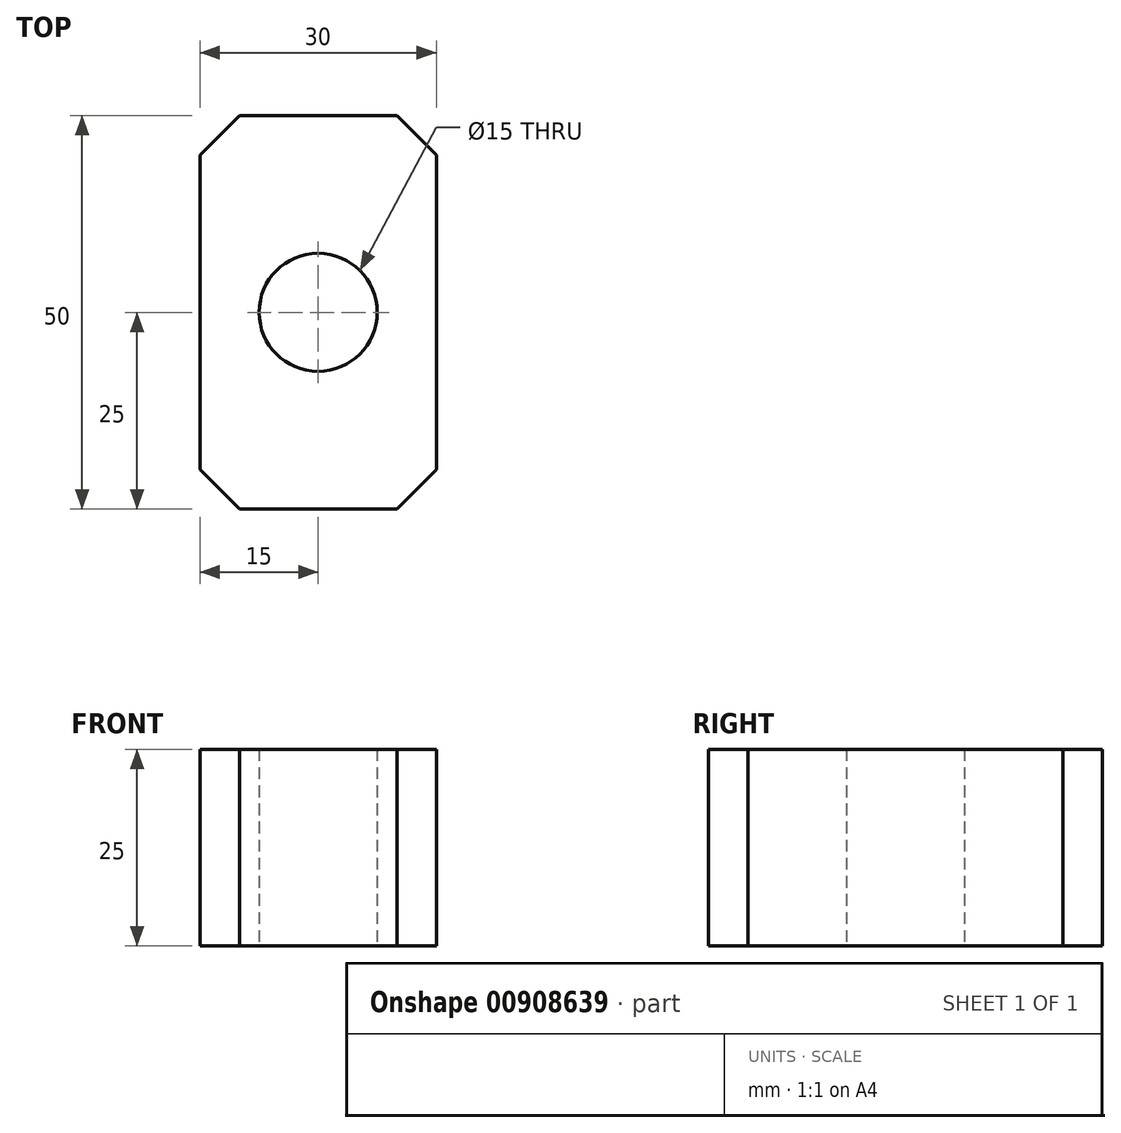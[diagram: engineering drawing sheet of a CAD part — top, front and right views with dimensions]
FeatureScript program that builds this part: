
annotation { "Feature Type Name" : "Feature", "Feature Type Description" : "" }
export const myFeature = defineFeature(function(context is Context, id is Id, definition is map)
    precondition{}
    {
        {
            var Q0;
            Q0=qCreatedBy(makeId("Top.planeOp"),FACE);
            var sketch = newSketch(context, id + "F0", { "sketchPlane" : qUnion([Q0])});
            skLineSegment(sketch, "E0.bottom", {"start": v(-15, 25) * mm, "end": v(15, 25) * mm});
            skLineSegment(sketch, "E0.top", {"start": v(-15, -25) * mm, "end": v(15, -25) * mm});
            skLineSegment(sketch, "E0.left", {"start": v(-15, 25) * mm, "end": v(-15, -25) * mm});
            skLineSegment(sketch, "E0.right", {"start": v(15, 25) * mm, "end": v(15, -25) * mm});
            skLineSegment(sketch, "E1", {"start": v(-15, 25) * mm, "end": v(15, -25) * mm, "construction": true});
            skCircle(sketch, "E2", {"center": v(0, 0) * mm, "radius": 7.5 * mm});
            skSolve(sketch);
        }
        {
            var Q0;
            Q0 = qSketchRegion(id + "F0", true);
            extrude(context, id + "F1", {"entities" : qUnion([Q0]), "depth" : 25 * mm, "offsetDistance" : 25 * mm});
        }
        {
            var Q0;
            Q0=makeQuery(id+"F1.opExtrude","SWEPT_EDGE",EDGE,{"disambiguationData":[OSD([sQuery(id+"F0.wireOp",EDGE,"E0.top"),sQuery(id+"F0.wireOp",EDGE,"E0.right")])]});
            var Q1;
            Q1=makeQuery(id+"F1.opExtrude","SWEPT_EDGE",EDGE,{"disambiguationData":[OSD([sQuery(id+"F0.wireOp",EDGE,"E0.top"),sQuery(id+"F0.wireOp",EDGE,"E0.left")])]});
            var Q2;
            Q2=makeQuery(id+"F1.opExtrude","SWEPT_EDGE",EDGE,{"disambiguationData":[OSD([sQuery(id+"F0.wireOp",EDGE,"E0.bottom"),sQuery(id+"F0.wireOp",EDGE,"E0.right")])]});
            var Q3;
            Q3=makeQuery(id+"F1.opExtrude","SWEPT_EDGE",EDGE,{"disambiguationData":[OSD([sQuery(id+"F0.wireOp",EDGE,"E0.bottom"),sQuery(id+"F0.wireOp",EDGE,"E0.left")])]});
            chamfer(context, id + "F2", {"entities" : qUnion([Q0, Q1, Q2, Q3]), "width" : 5 * mm, "tangentPropagation" : true});
        }
    });
